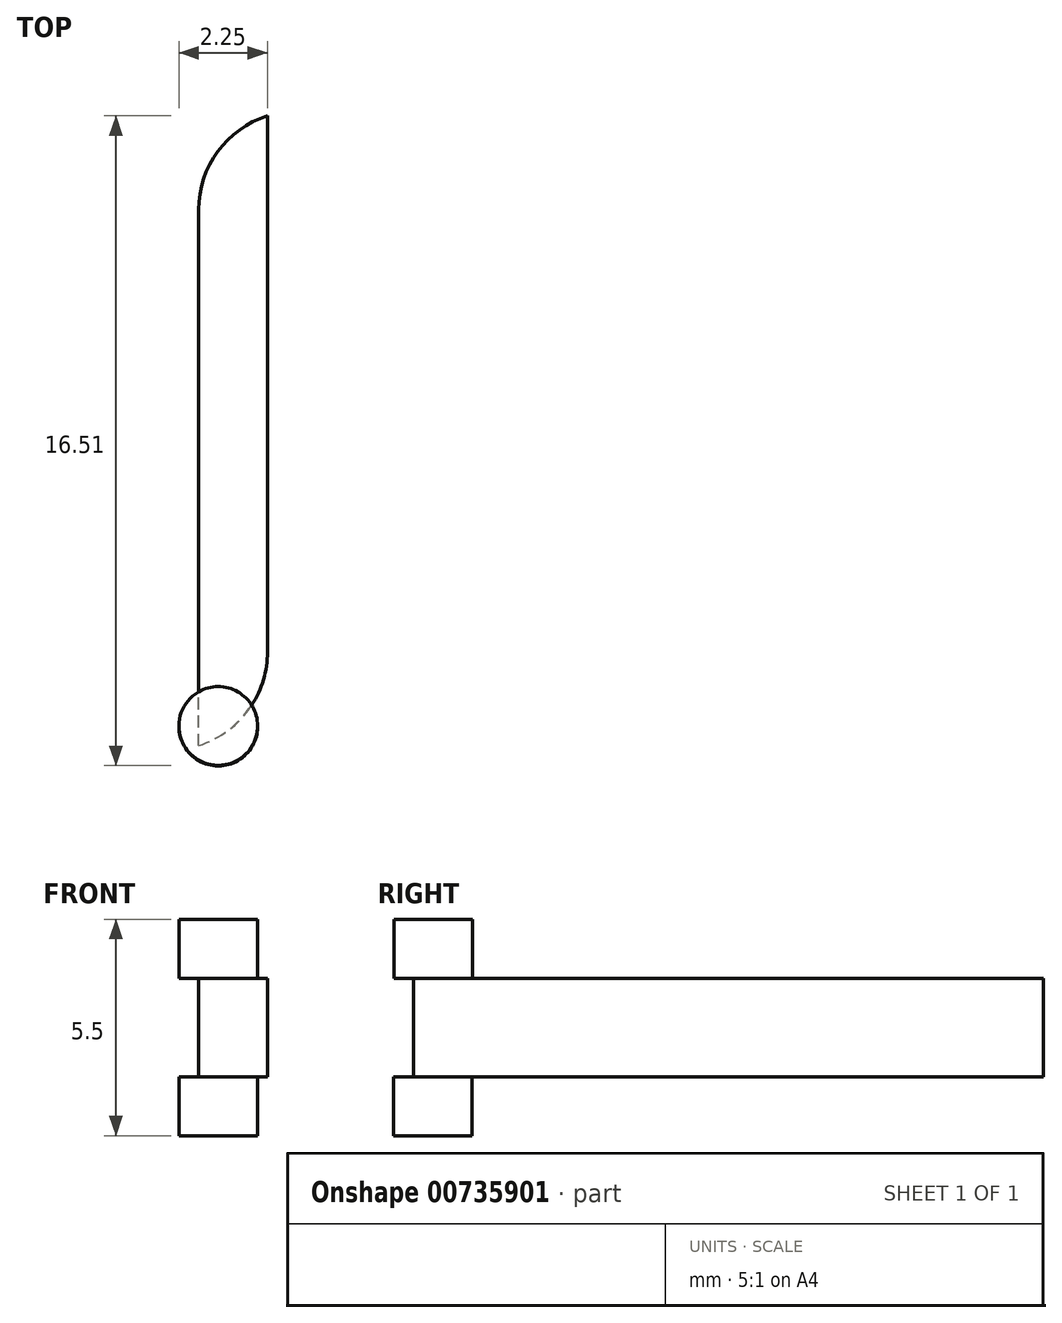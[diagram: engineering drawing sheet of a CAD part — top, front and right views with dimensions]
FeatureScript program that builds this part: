
annotation { "Feature Type Name" : "Feature", "Feature Type Description" : "" }
export const myFeature = defineFeature(function(context is Context, id is Id, definition is map)
    precondition{}
    {
        {
            var Q0;
            Q0=qCreatedBy(makeId("Right.planeOp"),FACE);
            var sketch = newSketch(context, id + "F0", { "sketchPlane" : qUnion([Q0])});
            skLineSegment(sketch, "E0.bottom", {"start": v(0, 0) * mm, "end": v(16, 0) * mm});
            skLineSegment(sketch, "E0.top", {"start": v(0, 2.5) * mm, "end": v(16, 2.5) * mm});
            skLineSegment(sketch, "E0.left", {"start": v(0, 0) * mm, "end": v(0, 2.5) * mm});
            skLineSegment(sketch, "E0.right", {"start": v(16, 0) * mm, "end": v(16, 2.5) * mm});
            skSolve(sketch);
        }
        {
            var Q0;
            Q0=makeQuery(id+"F0.imprint","IMPRINT",FACE,{"disambiguationData":[TD([[makeQuery(id+"F0.imprint","IMPRINT",EDGE,{"derivedFrom":sQuery(id+"F0.wireOp",EDGE,"E0.bottom")}),1.0]])]});
            extrude(context, id + "F1", {"entities" : qUnion([Q0]), "depth" : 1.75 * mm, "offsetDistance" : 25 * mm});
        }
        {
            var Q0;
            Q0=makeQuery(id+"F1.opExtrude","SWEPT_FACE",FACE,{"disambiguationData":[OSD([sQuery(id+"F0.wireOp",EDGE,"E0.bottom")])]});
            var sketch = newSketch(context, id + "F2", { "sketchPlane" : qUnion([Q0])});
            skCircle(sketch, "E1", {"center": v(0.5, -0.49) * mm, "radius": 1 * mm});
            skSolve(sketch);
        }
        {
            var Q0;
            Q0=makeQuery(id+"F1.opExtrude","SWEPT_FACE",FACE,{"disambiguationData":[OSD([sQuery(id+"F0.wireOp",EDGE,"E0.top")])]});
            var sketch = newSketch(context, id + "F3", { "sketchPlane" : qUnion([Q0])});
            skCircle(sketch, "E2", {"center": v(0.5, 0.5) * mm, "radius": 1 * mm});
            skSolve(sketch);
        }
        {
            var Q0;
            {var subQ1=sQuery(id+"F0.wireOp",EDGE,"E0.top");var subQ6=makeQuery(id+"F1.opExtrude","SWEPT_EDGE",EDGE,{"disambiguationData":[OSD([subQ1,sQuery(id+"F0.wireOp",EDGE,"E0.left")])]});Q0=makeQuery(id+"F3.imprint","IMPRINT",FACE,{"disambiguationData":[TD([[makeQuery(id+"F3.imprint","IMPRINT",EDGE,{"derivedFrom":subQ6}),1.0]])]});}
            var Q1;
            {var subQ1=sQuery(id+"F0.wireOp",EDGE,"E0.top");var subQ6=makeQuery(id+"F1.opExtrude","SWEPT_EDGE",EDGE,{"disambiguationData":[OSD([subQ1,sQuery(id+"F0.wireOp",EDGE,"E0.left")])]});Q1=makeQuery(id+"F3.imprint","IMPRINT",FACE,{"disambiguationData":[TD([[makeQuery(id+"F3.imprint","IMPRINT",EDGE,{"derivedFrom":subQ6}),-1.0]])]});}
            extrude(context, id + "F4", {"entities" : qUnion([Q0, Q1]), "operationType" : NewBodyOperationType.ADD, "depth" : 1.5 * mm, "offsetDistance" : 25 * mm});
        }
        {
            var Q0;
            {var subQ1=sQuery(id+"F0.wireOp",EDGE,"E0.bottom");var subQ6=makeQuery(id+"F1.opExtrude","SWEPT_EDGE",EDGE,{"disambiguationData":[OSD([subQ1,sQuery(id+"F0.wireOp",EDGE,"E0.left")])]});Q0=makeQuery(id+"F2.imprint","IMPRINT",FACE,{"disambiguationData":[TD([[makeQuery(id+"F2.imprint","IMPRINT",EDGE,{"derivedFrom":subQ6}),1.0]])]});}
            var Q1;
            {var subQ1=sQuery(id+"F0.wireOp",EDGE,"E0.bottom");var subQ6=makeQuery(id+"F1.opExtrude","SWEPT_EDGE",EDGE,{"disambiguationData":[OSD([subQ1,sQuery(id+"F0.wireOp",EDGE,"E0.left")])]});Q1=makeQuery(id+"F2.imprint","IMPRINT",FACE,{"disambiguationData":[TD([[makeQuery(id+"F2.imprint","IMPRINT",EDGE,{"derivedFrom":subQ6}),-1.0]])]});}
            extrude(context, id + "F5", {"entities" : qUnion([Q0, Q1]), "operationType" : NewBodyOperationType.ADD, "depth" : 1.5 * mm, "offsetDistance" : 25 * mm});
        }
        {
            var Q0;
            Q0=makeQuery(id+"F1.opExtrude","CAP_EDGE",EDGE,{"disambiguationData":[OSD([sQuery(id+"F0.wireOp",EDGE,"E0.right")])],"isStart":true});
            var Q1;
            Q1=makeQuery(id+"F1.opExtrude","CAP_EDGE",EDGE,{"disambiguationData":[OSD([sQuery(id+"F0.wireOp",EDGE,"E0.left")])],"isStart":false});
            fillet(context, id + "F6", {"entities" : qUnion([Q0, Q1]), "radius" : 2.5 * mm, "tangentPropagation" : true, "allowEdgeOverflow" : false});
        }
    });
